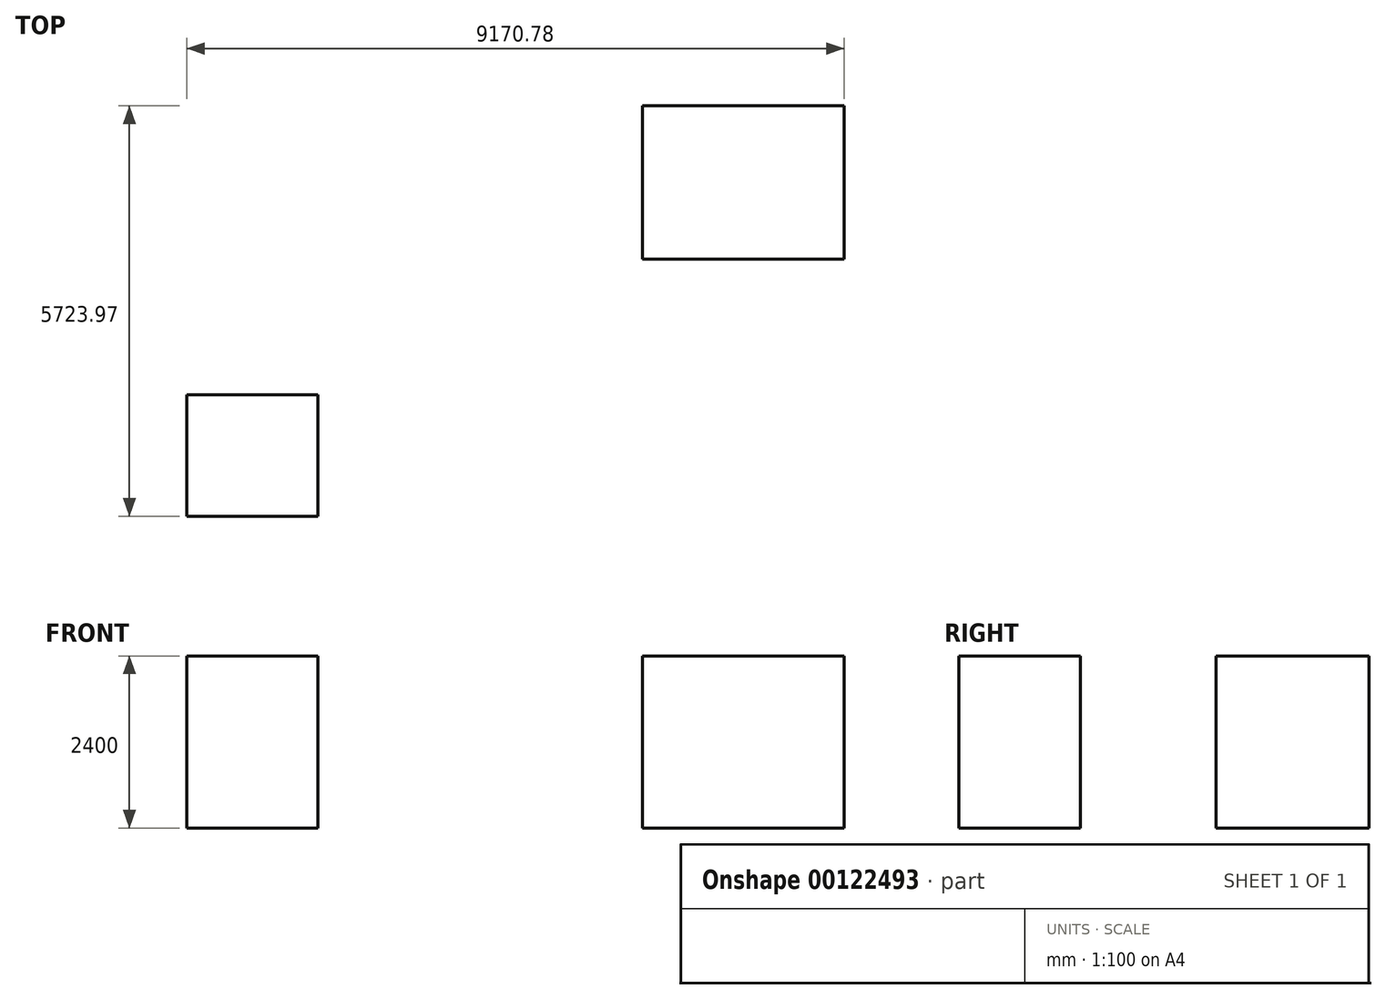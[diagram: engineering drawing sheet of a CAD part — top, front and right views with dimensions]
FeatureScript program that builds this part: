
annotation { "Feature Type Name" : "Feature", "Feature Type Description" : "" }
export const myFeature = defineFeature(function(context is Context, id is Id, definition is map)
    precondition{}
    {
        {
            var Q0;
            Q0=qCreatedBy(makeId("Top.planeOp"),FACE);
            var sketch = newSketch(context, id + "F0", { "sketchPlane" : qUnion([Q0])});
            skLineSegment(sketch, "E0", {"start": v(-4500, -11000) * mm, "end": v(0, -11000) * mm});
            skLineSegment(sketch, "E1", {"start": v(0, -11000) * mm, "end": v(4500, -11000) * mm});
            skLineSegment(sketch, "E2", {"start": v(4500, -11000) * mm, "end": v(4500, 0) * mm});
            skLineSegment(sketch, "E3", {"start": v(4500, 0) * mm, "end": v(0, 0) * mm});
            skLineSegment(sketch, "E4", {"start": v(0, 0) * mm, "end": v(-4500, 0) * mm});
            skLineSegment(sketch, "E5", {"start": v(-4500, 0) * mm, "end": v(-4500, -11000) * mm});
            skLineSegment(sketch, "E6", {"start": v(0, 0) * mm, "end": v(0, -11000) * mm, "construction": true});
            skSolve(sketch);
        }
        {
            var Q0;
            Q0=sQuery(id+"F0.wireOp",EDGE,"E0");
            var Q1;
            Q1=sQuery(id+"F0.wireOp",EDGE,"E1");
            var Q2;
            Q2=sQuery(id+"F0.wireOp",EDGE,"E5");
            var Q3;
            Q3=sQuery(id+"F0.wireOp",EDGE,"E4");
            var Q4;
            Q4=sQuery(id+"F0.wireOp",EDGE,"E2");
            extrude(context, id + "F1", {"bodyType" : ToolBodyType.SURFACE, "surfaceEntities" : qUnion([Q0, Q1, Q2, Q3, Q4]), "depth" : 4500 * mm});
        }
        {
            var Q0;
            Q0=qCreatedBy(makeId("Top.planeOp"),FACE);
            var sketch = newSketch(context, id + "F2", { "sketchPlane" : qUnion([Q0])});
            skLineSegment(sketch, "E7.bottom", {"start": v(-1830.77, -11000) * mm, "end": v(0, -11000) * mm});
            skLineSegment(sketch, "E7.top", {"start": v(-1830.77, -9304.85) * mm, "end": v(0, -9304.85) * mm});
            skLineSegment(sketch, "E7.left", {"start": v(-1830.77, -11000) * mm, "end": v(-1830.77, -9304.85) * mm});
            skLineSegment(sketch, "E7.right", {"start": v(0, -11000) * mm, "end": v(0, -9304.85) * mm});
            skLineSegment(sketch, "E8", {"start": v(0, 0) * mm, "end": v(0, -11000) * mm, "construction": true});
            skLineSegment(sketch, "E9.bottom", {"start": v(4526.06, -7411.93) * mm, "end": v(7340.01, -7411.93) * mm});
            skLineSegment(sketch, "E9.top", {"start": v(4526.06, -5276.03) * mm, "end": v(7340.01, -5276.03) * mm});
            skLineSegment(sketch, "E9.left", {"start": v(4526.06, -7411.93) * mm, "end": v(4526.06, -5276.03) * mm});
            skLineSegment(sketch, "E9.right", {"start": v(7340.01, -7411.93) * mm, "end": v(7340.01, -5276.03) * mm});
            skSolve(sketch);
        }
        {
            var Q0;
            Q0=makeQuery(id+"F2.imprint","IMPRINT",FACE,{"disambiguationData":[TD([[makeQuery(id+"F2.imprint","IMPRINT",EDGE,{"derivedFrom":sQuery(id+"F2.wireOp",EDGE,"E7.bottom")}),1.0]])]});
            var Q1;
            Q1=makeQuery(id+"F2.imprint","IMPRINT",FACE,{"disambiguationData":[TD([[makeQuery(id+"F2.imprint","IMPRINT",EDGE,{"derivedFrom":sQuery(id+"F2.wireOp",EDGE,"E9.bottom")}),1.0]])]});
            var Q2;
            Q2=sQuery(id+"F2.wireOp",EDGE,"E7.top");
            var Q3;
            Q3=sQuery(id+"F2.wireOp",EDGE,"E7.right");
            var Q4;
            Q4=sQuery(id+"F2.wireOp",EDGE,"E7.left");
            extrude(context, id + "F3", {"entities" : qUnion([Q0, Q1]), "surfaceEntities" : qUnion([Q2, Q3, Q4]), "depth" : 2400 * mm});
        }
    });
